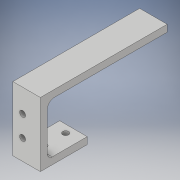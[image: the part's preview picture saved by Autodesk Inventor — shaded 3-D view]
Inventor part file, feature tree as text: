
AUTODESK INVENTOR PART (.ipt)
format: ipt  version: 2019 (Build 230136000, 136)  size: 141,824 bytes
history: native  units: in
note: dims shown in document units (in); Inventor stores cm internally (conversion verified against a paired STEP export)
features: extrude x3, sketch x3, fillet x2
ambient origin geometry x8: Origin, YZ Plane, XZ Plane, XY Plane, X Axis, Y Axis, Z Axis, Center Point
bodies: Solid1 (feature_tree)
feature tree (8):
  extrude  "Extrusion1"  Depth=0.85in
  extrude  "Extrusion2"  Depth=0.125in
  extrude  "Extrusion3"  Depth=0.125in
  fillet  "Fillet1"  Radius=2.3in
  fillet  "Fillet2"  Radius=0.107in
  sketch  "Sketch1"  dims[d0=0.125in d1=0.85in]
  sketch  "Sketch2"  dims[d2=0.5in d3=0.0in d4=0.125in]
  sketch  "Sketch3"  dims[d5=1.165in d6=0.125in d7=2.3in d8=0.107in d9=0.107in d10=0.322in d11=0.322in d12=0.379in d13=1.0in d14=0.0in d15=0.107in d16=0.107in d17=0.25in d18=0.25in d19=1.0in d20=0.0in d21=0.125in d22=0.09in d23=0.394in]
